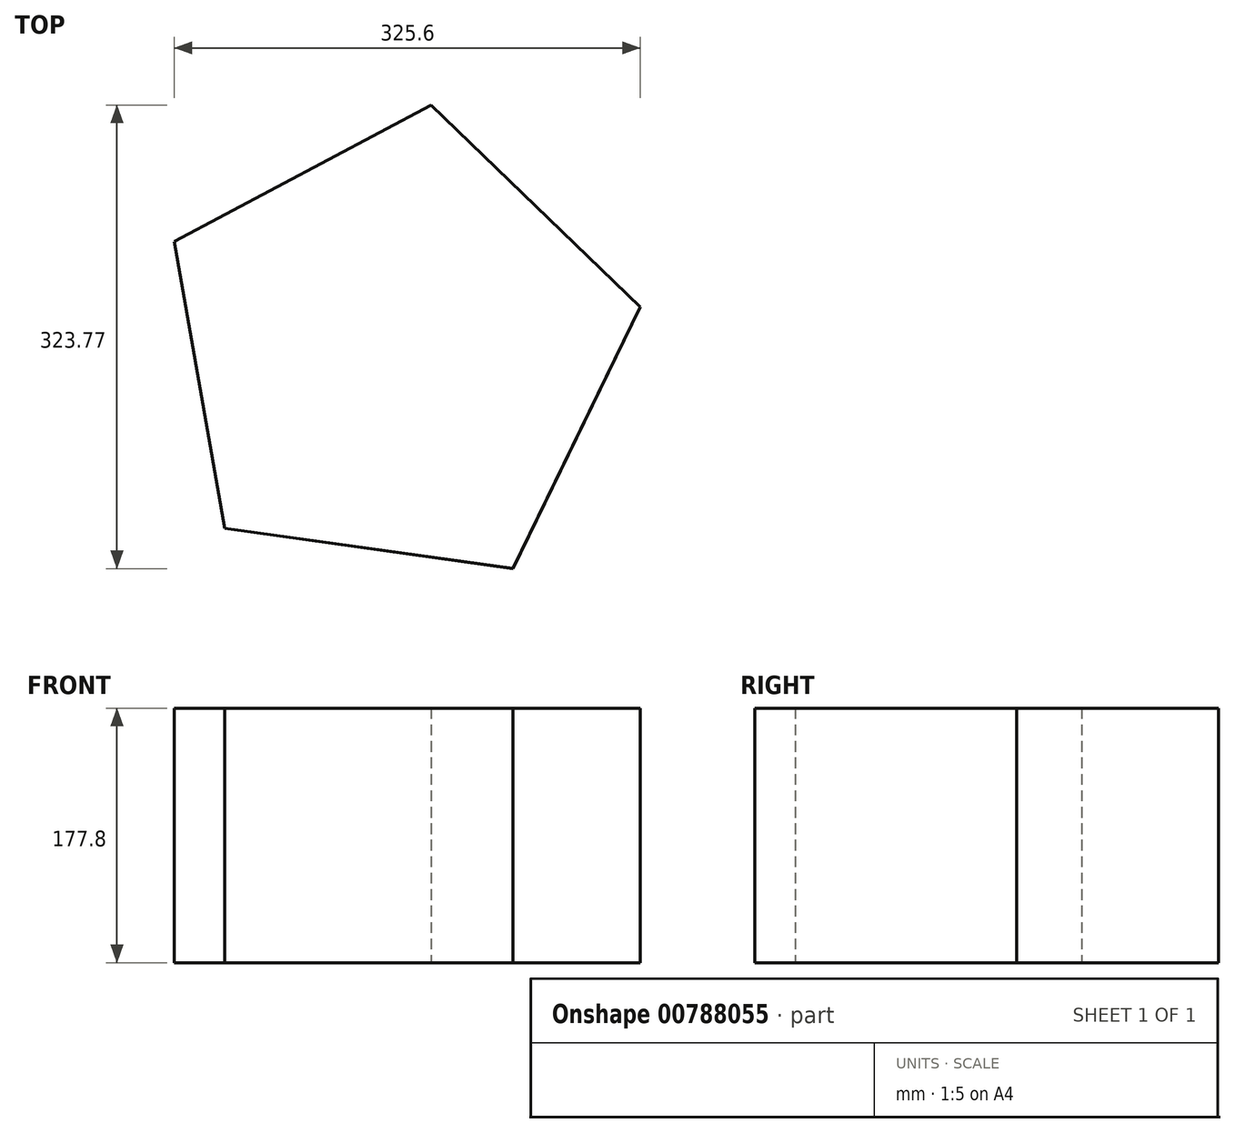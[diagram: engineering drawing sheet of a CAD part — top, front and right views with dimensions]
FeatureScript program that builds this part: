
annotation { "Feature Type Name" : "Feature", "Feature Type Description" : "" }
export const myFeature = defineFeature(function(context is Context, id is Id, definition is map)
    precondition{}
    {
        {
            var Q0;
            Q0=qCreatedBy(makeId("Top.planeOp"),FACE);
            var sketch = newSketch(context, id + "F0", { "sketchPlane" : qUnion([Q0])});
            skCircle(sketch, "E0.cCircle", {"center": v(0, 0) * mm, "radius": 139.84 * mm, "construction": true});
            skLineSegment(sketch, "E0.0", {"start": v(-155.38, 75.72) * mm, "end": v(24, 171.18) * mm});
            skLineSegment(sketch, "E0.1", {"start": v(24, 171.18) * mm, "end": v(170.22, 30.07) * mm});
            skLineSegment(sketch, "E0.2", {"start": v(170.22, 30.07) * mm, "end": v(81.2, -152.6) * mm});
            skLineSegment(sketch, "E0.3", {"start": v(81.2, -152.6) * mm, "end": v(-120.03, -124.38) * mm});
            skLineSegment(sketch, "E0.4", {"start": v(-120.03, -124.38) * mm, "end": v(-155.38, 75.72) * mm});
            skPoint(sketch, "E0.0.midPoint", {"position": v(-65.7, 123.45) * mm});
            skSolve(sketch);
        }
        {
            var Q0;
            Q0 = qSketchRegion(id + "F0", true);
            extrude(context, id + "F1", {"entities" : qUnion([Q0]), "depth" : 177.8 * mm, "offsetDistance" : 25.4 * mm});
        }
        {
            var Q0;
            Q0=makeQuery(id+"F1.opExtrude","CAP_FACE",FACE,{"disambiguationData":[OSD([sQuery(id+"F0.wireOp",EDGE,"E0.0"),sQuery(id+"F0.wireOp",EDGE,"E0.1"),sQuery(id+"F0.wireOp",EDGE,"E0.2"),sQuery(id+"F0.wireOp",EDGE,"E0.3"),sQuery(id+"F0.wireOp",EDGE,"E0.4")])],"isStart":false});
            shell(context, id + "F2", {"entities" : qUnion([Q0]), "thickness" : 3 / 177.8 * mm});
        }
    });
